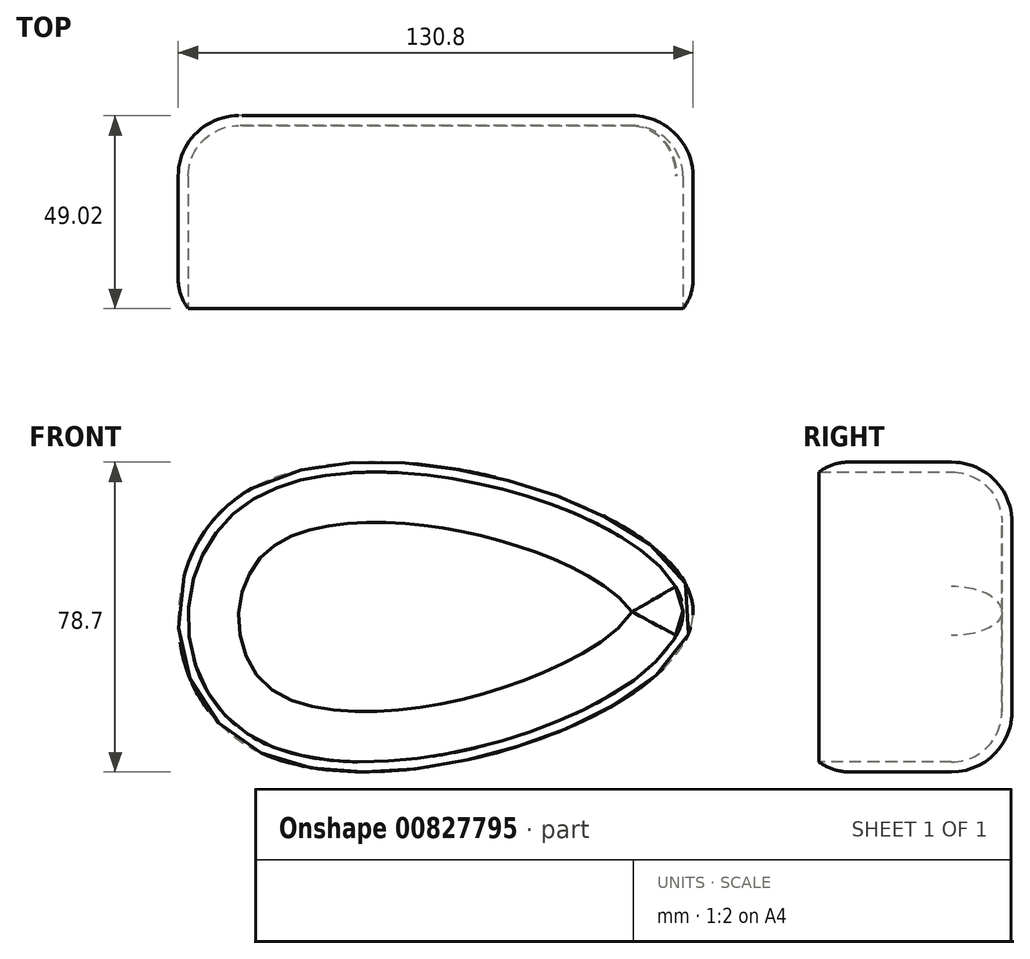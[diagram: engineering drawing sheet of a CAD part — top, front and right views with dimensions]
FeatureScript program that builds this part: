
annotation { "Feature Type Name" : "Feature", "Feature Type Description" : "" }
export const myFeature = defineFeature(function(context is Context, id is Id, definition is map)
    precondition{}
    {
        {
            var Q0;
            Q0=qCreatedBy(makeId("Front.planeOp"),FACE);
            var sketch = newSketch(context, id + "F0", { "sketchPlane" : qUnion([Q0])});
            skFitSpline(sketch, "E0", {"points": [v(-48.69, 31.16) * mm, v(63.42, 0) * mm, v(-48.03, -35.19) * mm, v(-48.69, 31.16) * mm]});
            skSolve(sketch);
        }
        {
            var Q0;
            Q0 = qSketchRegion(id + "F0", true);
            extrude(context, id + "F1", {"entities" : qUnion([Q0]), "oppositeDirection" : true, "depth" : 49.02 * mm, "offsetDistance" : 25.4 * mm});
        }
        {
            var Q0;
            Q0=makeQuery(id+"F1.opExtrude","CAP_EDGE",EDGE,{"disambiguationData":[OSD([sQuery(id+"F0.wireOp",EDGE,"E0")])],"isStart":false});
            fillet(context, id + "F2", {"entities" : qUnion([Q0]), "radius" : 15.33 * mm, "tangentPropagation" : true, "allowEdgeOverflow" : false});
        }
        {
            var Q0;
            Q0=makeQuery(id+"F1.opExtrude","CAP_FACE",FACE,{"disambiguationData":[OSD([sQuery(id+"F0.wireOp",EDGE,"E0")])],"isStart":true});
            shell(context, id + "F3", {"entities" : qUnion([Q0]), "thickness" : 2.54 * mm});
        }
        {
            var Q0;
            Q0=makeQuery(id+"F1.opExtrude","CAP_EDGE",EDGE,{"disambiguationData":[OSD([sQuery(id+"F0.wireOp",EDGE,"E0")])],"isStart":true});
            fillet(context, id + "F4", {"entities" : qUnion([Q0]), "radius" : 12.26 * mm, "tangentPropagation" : true, "allowEdgeOverflow" : false});
        }
    });
